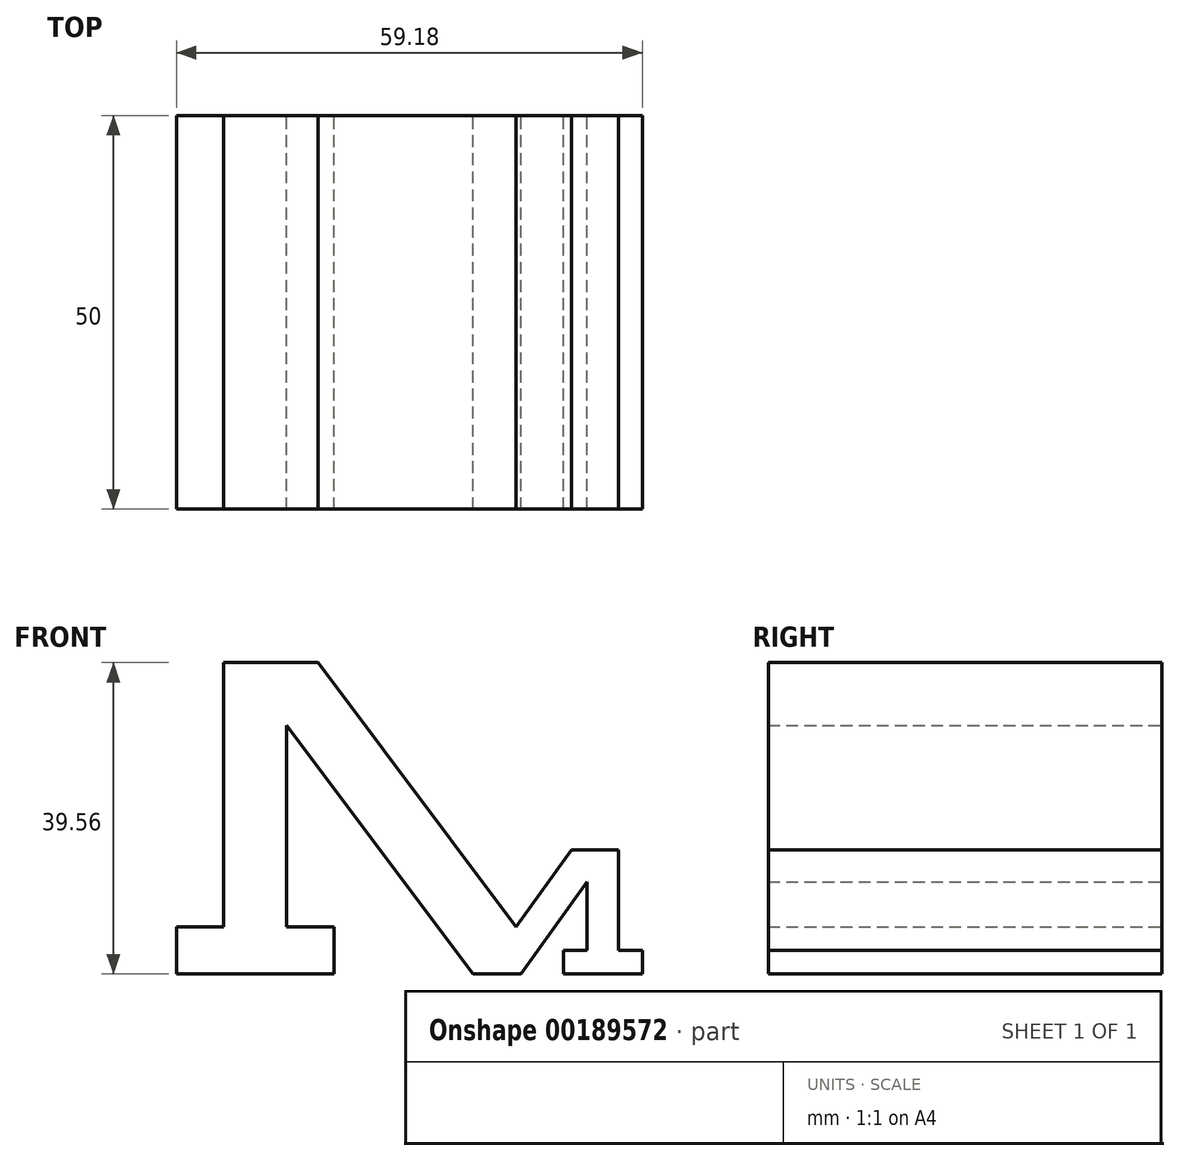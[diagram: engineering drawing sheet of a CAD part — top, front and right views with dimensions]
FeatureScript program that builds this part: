
annotation { "Feature Type Name" : "Feature", "Feature Type Description" : "" }
export const myFeature = defineFeature(function(context is Context, id is Id, definition is map)
    precondition{}
    {
        {
            var Q0;
            Q0=qCreatedBy(makeId("Front.planeOp"),FACE);
            var sketch = newSketch(context, id + "F0", { "sketchPlane" : qUnion([Q0])});
            skLineSegment(sketch, "E0", {"start": v(-43.17, 0) * mm, "end": v(-43.17, 6) * mm});
            skLineSegment(sketch, "E1", {"start": v(-43.17, 6) * mm, "end": v(-37.17, 6) * mm});
            skLineSegment(sketch, "E2", {"start": v(-37.17, 6) * mm, "end": v(-37.17, 39.56) * mm});
            skLineSegment(sketch, "E3", {"start": v(-37.17, 39.56) * mm, "end": v(-25.17, 39.56) * mm});
            skLineSegment(sketch, "E4", {"start": v(-25.17, 39.56) * mm, "end": v(0, 6) * mm});
            skLineSegment(sketch, "E5", {"start": v(0, 6) * mm, "end": v(7.01, 15.78) * mm});
            skLineSegment(sketch, "E6", {"start": v(13.01, 15.78) * mm, "end": v(13.01, 3) * mm});
            skLineSegment(sketch, "E7", {"start": v(16.01, 0) * mm, "end": v(6.01, 0) * mm});
            skLineSegment(sketch, "E8", {"start": v(-43.17, 0) * mm, "end": v(-23.17, 0) * mm});
            skLineSegment(sketch, "E9", {"start": v(-23.17, 0) * mm, "end": v(-23.17, 6) * mm});
            skLineSegment(sketch, "E10", {"start": v(-23.17, 6) * mm, "end": v(-29.17, 6) * mm});
            skLineSegment(sketch, "E11", {"start": v(-29.17, 6) * mm, "end": v(-29.17, 31.56) * mm});
            skLineSegment(sketch, "E12", {"start": v(-29.17, 31.56) * mm, "end": v(-5.5, 0) * mm});
            skLineSegment(sketch, "E13", {"start": v(9.01, 11.7) * mm, "end": v(0.62, 0) * mm});
            skLineSegment(sketch, "E14", {"start": v(0.62, 0) * mm, "end": v(-5.5, 0) * mm});
            skLineSegment(sketch, "E15", {"start": v(9.01, 11.7) * mm, "end": v(9.01, 3) * mm});
            skLineSegment(sketch, "E16", {"start": v(7.01, 15.78) * mm, "end": v(13.01, 15.78) * mm});
            skLineSegment(sketch, "E17", {"start": v(9.01, 3) * mm, "end": v(6.01, 3) * mm});
            skLineSegment(sketch, "E18", {"start": v(6.01, 3) * mm, "end": v(6.01, 0) * mm});
            skLineSegment(sketch, "E19", {"start": v(13.01, 3) * mm, "end": v(16.01, 3) * mm});
            skLineSegment(sketch, "E20", {"start": v(16.01, 3) * mm, "end": v(16.01, 0) * mm});
            skSolve(sketch);
        }
        {
            var Q0;
            Q0=makeQuery(id+"F0.imprint","IMPRINT",FACE,{"disambiguationData":[TD([[makeQuery(id+"F0.imprint","IMPRINT",EDGE,{"derivedFrom":sQuery(id+"F0.wireOp",EDGE,"E0")}),-1.0]])]});
            extrude(context, id + "F1", {"entities" : qUnion([Q0]), "endBound" : BoundingType.SYMMETRIC, "depth" : 50 * mm});
        }
    });
